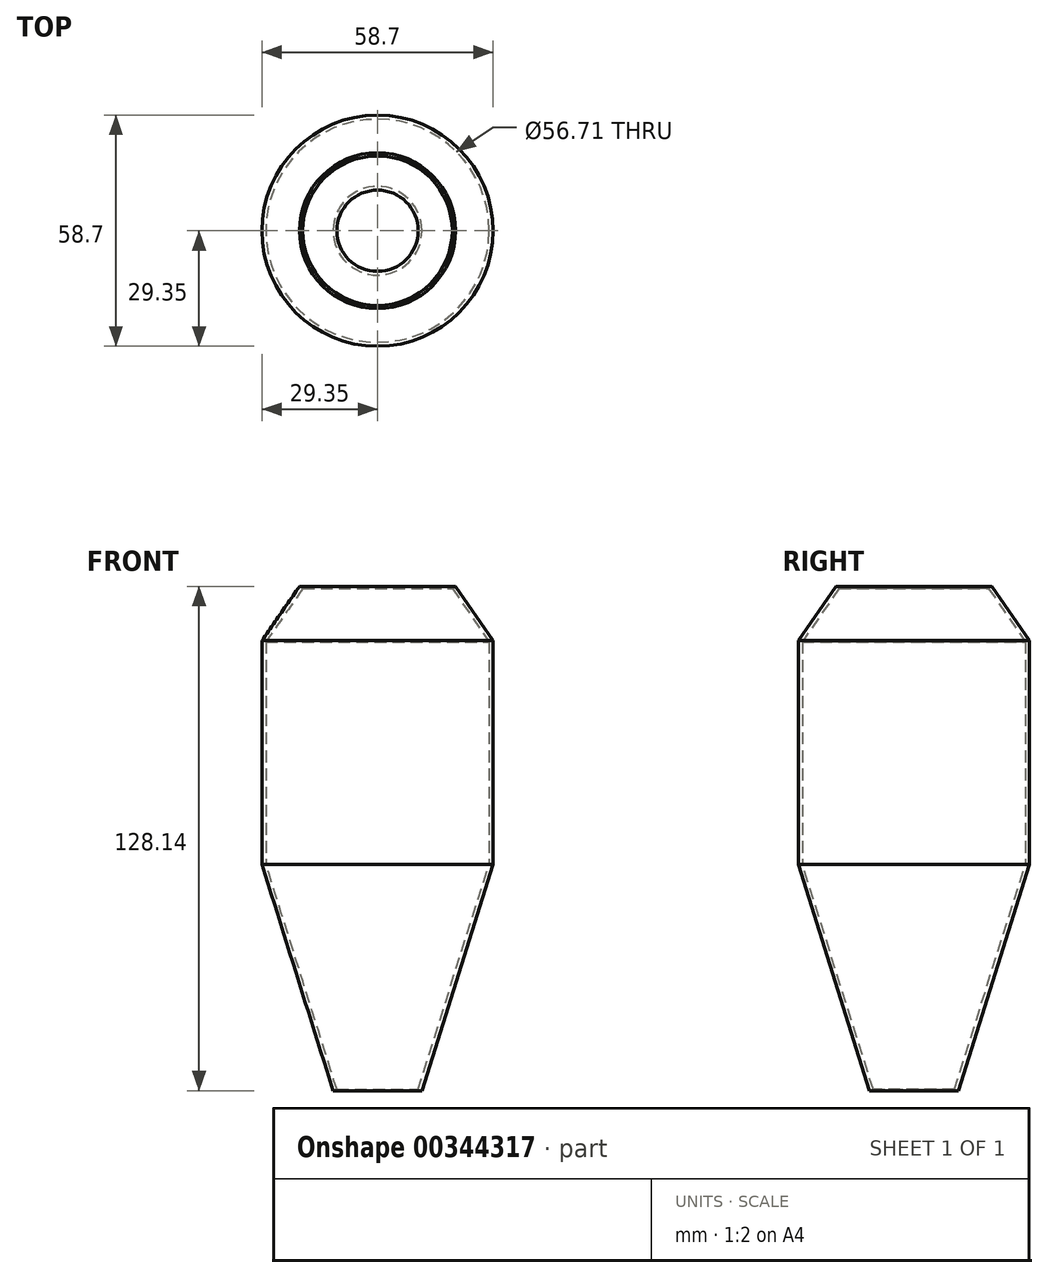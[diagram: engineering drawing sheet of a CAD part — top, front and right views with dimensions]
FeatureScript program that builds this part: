
annotation { "Feature Type Name" : "Feature", "Feature Type Description" : "" }
export const myFeature = defineFeature(function(context is Context, id is Id, definition is map)
    precondition{}
    {
        {
            var Q0;
            Q0=qCreatedBy(makeId("Front.planeOp"),FACE);
            var sketch = newSketch(context, id + "F0", { "sketchPlane" : qUnion([Q0])});
            skLineSegment(sketch, "E0", {"start": v(-11.28, 0) * mm, "end": v(-29.35, 57.48) * mm});
            skLineSegment(sketch, "E1", {"start": v(-29.35, 57.48) * mm, "end": v(-29.35, 114.34) * mm});
            skLineSegment(sketch, "E2", {"start": v(-29.35, 114.34) * mm, "end": v(-19.82, 128.14) * mm});
            skLineSegment(sketch, "E3.0", {"start": v(-28.35, 114.03) * mm, "end": v(-19, 127.58) * mm});
            skLineSegment(sketch, "E3.1", {"start": v(-28.35, 57.63) * mm, "end": v(-28.35, 114.03) * mm});
            skLineSegment(sketch, "E3.2", {"start": v(-10.32, 0.3) * mm, "end": v(-28.35, 57.63) * mm});
            skLineSegment(sketch, "E4", {"start": v(-19.82, 128.14) * mm, "end": v(-19, 127.58) * mm});
            skLineSegment(sketch, "E5", {"start": v(-11.28, 0) * mm, "end": v(-10.32, 0.3) * mm});
            skLineSegment(sketch, "E6", {"start": v(0, 0) * mm, "end": v(0, 137.93) * mm, "construction": true});
            skSolve(sketch);
        }
        {
            var Q0;
            Q0=makeQuery(id+"F0.imprint","IMPRINT",FACE,{"disambiguationData":[TD([[makeQuery(id+"F0.imprint","IMPRINT",EDGE,{"derivedFrom":sQuery(id+"F0.wireOp",EDGE,"E0")}),-1.0]])]});
            var Q1;
            Q1=sQuery(id+"F0.wireOp",EDGE,"E6");
            revolve(context, id + "F1", {"entities" : qUnion([Q0]), "axis" : qUnion([Q1]), "revolveType" : RevolveType.FULL});
        }
    });
